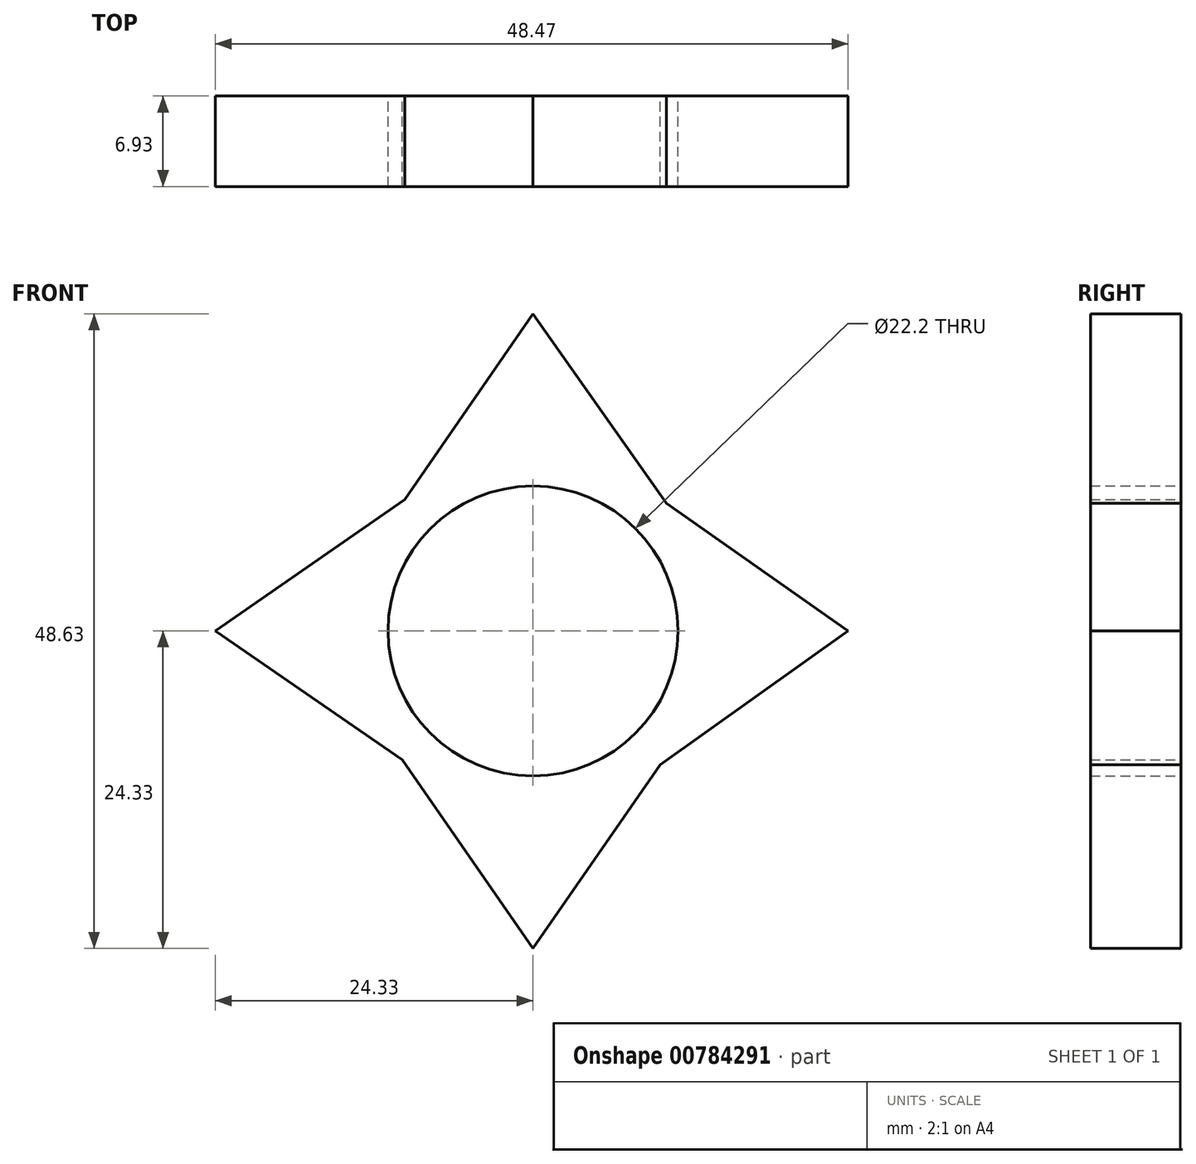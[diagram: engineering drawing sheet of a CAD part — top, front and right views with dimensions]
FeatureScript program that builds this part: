
annotation { "Feature Type Name" : "Feature", "Feature Type Description" : "" }
export const myFeature = defineFeature(function(context is Context, id is Id, definition is map)
    precondition{}
    {
        {
            var Q0;
            Q0=qCreatedBy(makeId("Front.planeOp"),FACE);
            var sketch = newSketch(context, id + "F0", { "sketchPlane" : qUnion([Q0])});
            skLineSegment(sketch, "E0", {"start": v(0, 0) * mm, "end": v(0, 24.3) * mm});
            skLineSegment(sketch, "E1", {"start": v(0, 24.3) * mm, "end": v(0, -24.33) * mm});
            skLineSegment(sketch, "E2", {"start": v(0, 0) * mm, "end": v(-24.33, 0) * mm});
            skLineSegment(sketch, "E3", {"start": v(0, 0) * mm, "end": v(24.14, 0) * mm});
            skCircle(sketch, "E4", {"center": v(0, 0) * mm, "radius": 11.1 * mm});
            skLineSegment(sketch, "E5", {"start": v(0.06, 0) * mm, "end": v(0, -0.06) * mm});
            skLineSegment(sketch, "E6", {"start": v(0, 0) * mm, "end": v(0.03, -0.03) * mm});
            skCircle(sketch, "E7", {"center": v(0.06, 0) * mm, "radius": 14.1 * mm, "construction": true});
            skLineSegment(sketch, "E8", {"start": v(0, 24.3) * mm, "end": v(-9.81, 10.07) * mm});
            skLineSegment(sketch, "E9", {"start": v(-24.33, 0) * mm, "end": v(-9.81, 10.07) * mm});
            skLineSegment(sketch, "E10", {"start": v(-24.33, 0) * mm, "end": v(-10.02, -9.86) * mm});
            skLineSegment(sketch, "E11", {"start": v(-10.02, -9.86) * mm, "end": v(0, -24.33) * mm});
            skLineSegment(sketch, "E12", {"start": v(0, -24.33) * mm, "end": v(9.76, -10.24) * mm});
            skLineSegment(sketch, "E13", {"start": v(9.76, -10.24) * mm, "end": v(24.14, 0) * mm});
            skLineSegment(sketch, "E14", {"start": v(24.14, 0) * mm, "end": v(10.22, 9.79) * mm});
            skLineSegment(sketch, "E15", {"start": v(10.22, 9.79) * mm, "end": v(0, 24.3) * mm});
            skSolve(sketch);
        }
        {
            var Q0;
            Q0 = qSketchRegion(id + "F0", true);
            extrude(context, id + "F1", {"entities" : qUnion([Q0]), "depth" : 6.93 * mm, "offsetDistance" : 25.4 * mm});
        }
    });
